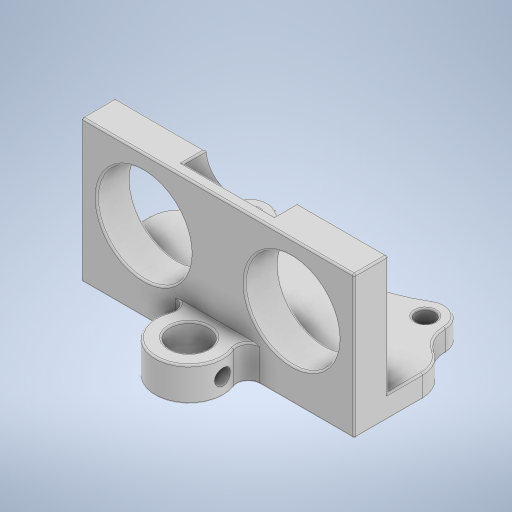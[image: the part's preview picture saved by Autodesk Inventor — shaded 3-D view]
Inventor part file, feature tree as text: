
AUTODESK INVENTOR PART (.ipt)
format: ipt  version: 2023 (Build 270158000, 158)  size: 481,280 bytes
history: native  units: in
note: dims shown in document units (in); Inventor stores cm internally (conversion verified against a paired STEP export)
features: extrude x7, sketch x7, fillet x1
ambient origin geometry x8: Origin, YZ Plane, XZ Plane, XY Plane, X Axis, Y Axis, Z Axis, Center Point
bodies: Solid1 (feature_tree)
feature tree (15):
  extrude  "Extrusion1"  Depth=1.2205in
  extrude  "Extrusion3"  Depth=0.1969in
  extrude  "Extrusion4"  Depth=0.8268in
  extrude  "Extrusion5"  Depth=0.2677in
  extrude  "Extrusion6"  Depth=0.1969in
  extrude  "Extrusion7"  Depth=0.1969in
  extrude  "Extrusion8"  Depth=0.0118in
  fillet  "Fillet1"  Radius=0.8268in
  sketch  "Sketch1"  dims[d0=0.1299in d1=1.2205in]
  sketch  "Sketch3"  dims[d3=0.1378in d6=0.1969in]
  sketch  "Sketch4"  dims[d8=0.1181in d10=0.8268in]
  sketch  "Sketch5"  dims[d11=0.4724in d12=0.2677in]
  sketch  "Sketch6"  dims[d13=0.1969in d14=0.2362in d15=1.8898in]
  sketch  "Sketch7"  dims[d16=0.1969in d17=0.0787in]
  sketch  "Sketch8"  dims[d19=0.1575in d20=0.0in d23=0.2362in d24=0.8268in d25=0.0in d26=1.0236in d27=0.6496in d28=0.5118in d29=0.3937in d30=0.0in d31=0.0in d32=0.4528in d33=0.1969in d34=0.3839in d35=0.1575in d36=0.0in d37=0.6299in d38=0.3543in d39=0.1575in d40=0.0in d41=0.0787in d42=0.0in d43=0.1102in d44=0.1181in d45=0.9449in d46=0.0in d47=0.0118in]
